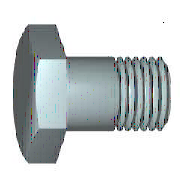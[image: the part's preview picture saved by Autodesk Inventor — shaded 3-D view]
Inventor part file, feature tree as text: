
AUTODESK INVENTOR PART (.ipt)
format: ipt  version: 2020 (Build 240168000, 168)  size: 189,952 bytes
history: native  units: mm (DEFAULTED — no unit token found)
features: sketch x3, other x1, extrude x1, chamfer x1, plane x1
ambient origin geometry x7: Origin, YZ Plane, XZ Plane, X Axis, Y Axis, Z Axis, Center Point
bodies: Solid1 (feature_tree)
feature tree (7):
  other  "轴承体"
  extrude  "头"  Depth=30.0mm
  chamfer  "倒角1"  Distance=6.9mm
  plane  "Work Plane1"
  sketch  "草图1"  dims[d0=45.0mm d1=30.0mm]
  sketch  "草图2"  dims[d2=12.0mm]
  sketch  "草图4"  dims[d12=90.0deg d3=6.9mm d4=0.0mm d5=30.0deg d21=90.0deg d6=0.920175mm d7=0.920275mm d8=0.0mm d9=0.6001mm d10=16.6mm d11=18.0mm d13=0.920275mm d14=12.0mm d15=30.0mm d16=0.0mm d19=18.0mm d55=45.0deg d57=0.0mm d58=0.0mm]
